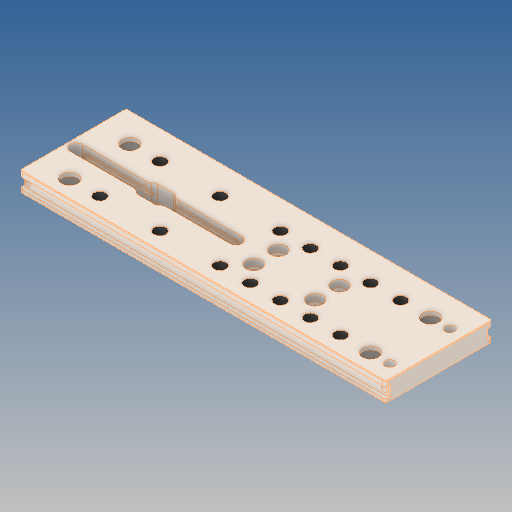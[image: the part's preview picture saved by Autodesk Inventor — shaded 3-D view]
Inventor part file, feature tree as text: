
AUTODESK INVENTOR PART (.ipt)
format: ipt  version: 2019 (Build 230136000, 136)  size: 286,720 bytes
history: native  units: mm
features: fillet x1
ambient origin geometry x8: Origin, YZ Plane, XZ Plane, XY Plane, X Axis, Y Axis, Z Axis, Center Point
bodies: Solid1 (feature_tree)
feature tree (1):
  fillet  "Fillet R = .020"  [1 undecoded]
note: 1 required parameter value undecoded (feature->parameter linkage not recoverable at this tier; creation-order binding heuristic only, values carry confidence <= 0.55)
